# Revit family: DuctPanel_ASI-Alpaco_Frameless
name_source: partatom
category: Generic Models
revit_build: Autodesk Revit 2015 (Build: 20140606_1530(x64)
units: mm (PartAtom-declared; Revit-internal decimal feet)

## types (2) — shared parameters
Assembly Code = C3010140
Bottom Join = No
Cover Panel Finish = <By Category>
Cover Panel Thickness = 0' - 0 1/2"
Default Elevation = 4' - 0"
Description = ASI Alpaco Panel
Fastener Offset = 0' - 1"
Flash Panel Finish = <By Category>
Flash Panel Thickness = 0' - 0 1/2"
FlashFrame Width = 0' - 6"
Keynote = 06 26 00
Left Join = No
Manufacturer = ASI-Alpaco
Model = Alpaco
Right Join = No
Top Join = No
URL = http://americanspecialties.com
zero-valued in all types: Cost

## type names
- Fixed Panel
- Access Panel
type visibility flags (boolean, named after types; folded from table):
- Fixed Panel: Yes: (none)
- Access Panel: Yes: Access Panel

## geometry (parser evidence)
native form markers: Sweep x2
no freeform markers — native parametric forms only
